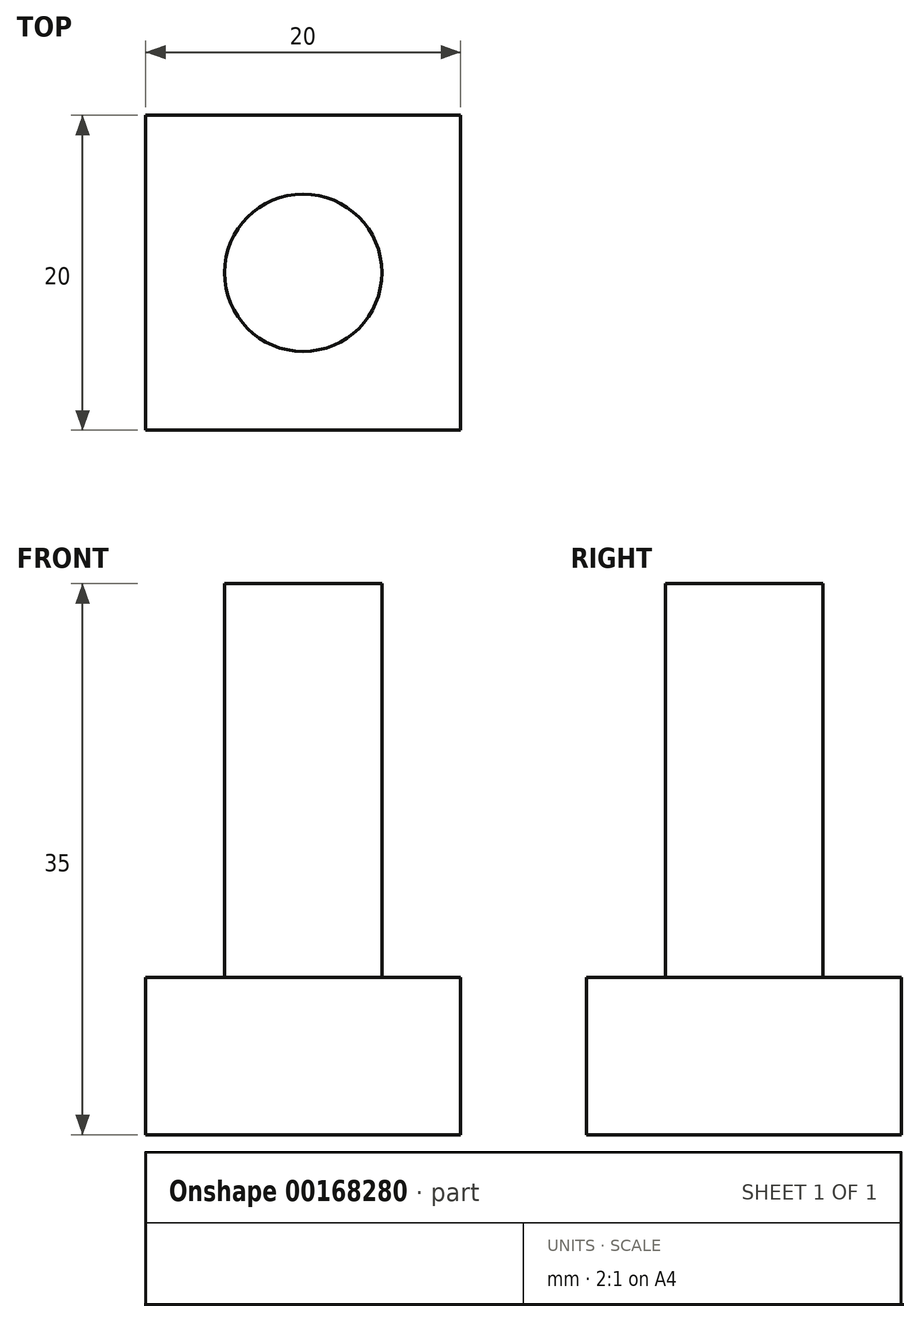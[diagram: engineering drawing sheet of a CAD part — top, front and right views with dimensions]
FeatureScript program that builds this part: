
annotation { "Feature Type Name" : "Feature", "Feature Type Description" : "" }
export const myFeature = defineFeature(function(context is Context, id is Id, definition is map)
    precondition{}
    {
        {
            var Q0;
            Q0=qCreatedBy(makeId("Top.planeOp"),FACE);
            var sketch = newSketch(context, id + "F0", { "sketchPlane" : qUnion([Q0])});
            skLineSegment(sketch, "E0.bottom", {"start": v(10, 10) * mm, "end": v(-10, 10) * mm});
            skLineSegment(sketch, "E0.top", {"start": v(10, -10) * mm, "end": v(-10, -10) * mm});
            skLineSegment(sketch, "E0.left", {"start": v(10, 10) * mm, "end": v(10, -10) * mm});
            skLineSegment(sketch, "E0.right", {"start": v(-10, 10) * mm, "end": v(-10, -10) * mm});
            skPoint(sketch, "E0.middle", {"position": v(0, 0) * mm});
            skSolve(sketch);
        }
        {
            var Q0;
            Q0=makeQuery(id+"F0.imprint","IMPRINT",FACE,{"disambiguationData":[TD([[makeQuery(id+"F0.imprint","IMPRINT",EDGE,{"derivedFrom":sQuery(id+"F0.wireOp",EDGE,"E0.bottom")}),1.0]])]});
            var Q1;
            Q1=qSketchRegion(id+"F0",true);
            extrude(context, id + "F1", {"entities" : qUnion([Q0, Q1]), "depth" : 10 * mm});
        }
        {
            var Q0;
            Q0=makeQuery(id+"F1.opExtrude","CAP_FACE",FACE,{"disambiguationData":[OSD([sQuery(id+"F0.wireOp",EDGE,"E0.bottom"),sQuery(id+"F0.wireOp",EDGE,"E0.top"),sQuery(id+"F0.wireOp",EDGE,"E0.left"),sQuery(id+"F0.wireOp",EDGE,"E0.right")])],"isStart":false});
            var sketch = newSketch(context, id + "F2", { "sketchPlane" : qUnion([Q0])});
            skCircle(sketch, "E1", {"center": v(0, 0) * mm, "radius": 5 * mm});
            skSolve(sketch);
        }
        {
            var Q0;
            Q0=qSketchRegion(id+"F2",true);
            extrude(context, id + "F3", {"entities" : qUnion([Q0]), "operationType" : NewBodyOperationType.ADD, "depth" : 25 * mm});
        }
    });
